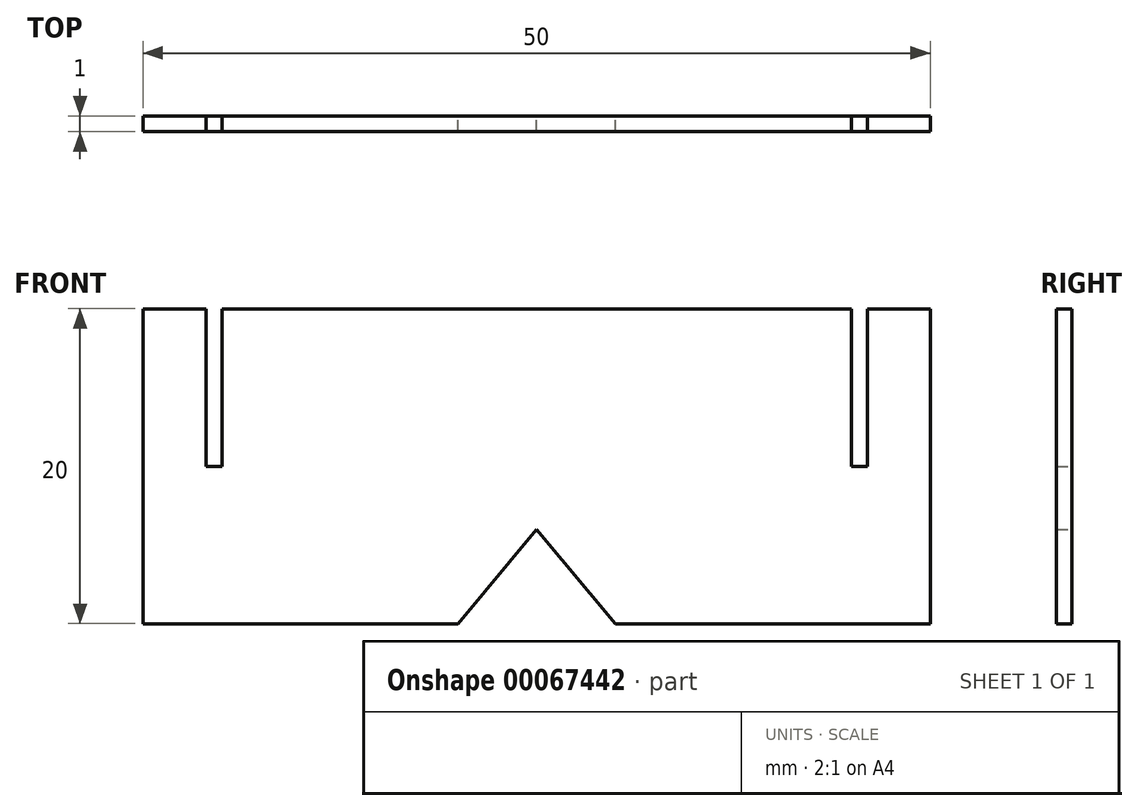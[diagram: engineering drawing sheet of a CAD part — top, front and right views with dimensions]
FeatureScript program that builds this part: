
annotation { "Feature Type Name" : "Feature", "Feature Type Description" : "" }
export const myFeature = defineFeature(function(context is Context, id is Id, definition is map)
    precondition{}
    {
        {
            var Q0;
            Q0=qCreatedBy(makeId("Front.planeOp"),FACE);
            var sketch = newSketch(context, id + "F0", { "sketchPlane" : qUnion([Q0])});
            skLineSegment(sketch, "E0.bottom", {"start": v(-29.64, 26.4) * mm, "end": v(-25.64, 26.4) * mm});
            skLineSegment(sketch, "E0.top", {"start": v(-29.64, 6.4) * mm, "end": v(-9.64, 6.4) * mm});
            skLineSegment(sketch, "E0.left", {"start": v(-29.64, 26.4) * mm, "end": v(-29.64, 6.4) * mm});
            skLineSegment(sketch, "E0.right", {"start": v(20.36, 26.4) * mm, "end": v(20.36, 6.4) * mm});
            skLineSegment(sketch, "E1.top", {"start": v(-25.64, 16.4) * mm, "end": v(-24.64, 16.4) * mm});
            skLineSegment(sketch, "E1.left", {"start": v(-25.64, 26.4) * mm, "end": v(-25.64, 16.4) * mm});
            skLineSegment(sketch, "E1.right", {"start": v(-24.64, 26.4) * mm, "end": v(-24.64, 16.4) * mm});
            skLineSegment(sketch, "E2.MirrorCS", {"start": v(15.36, 26.4) * mm, "end": v(15.36, 16.4) * mm});
            skLineSegment(sketch, "E3.MirrorCS", {"start": v(16.36, 26.4) * mm, "end": v(16.36, 16.4) * mm});
            skLineSegment(sketch, "E4.MirrorCS", {"start": v(16.36, 16.4) * mm, "end": v(15.36, 16.4) * mm});
            skPoint(sketch, "E5", {"position": v(-9.64, 6.4) * mm});
            skPoint(sketch, "E6", {"position": v(0.36, 6.4) * mm});
            skPoint(sketch, "E7", {"position": v(-4.64, 12.4) * mm});
            skLineSegment(sketch, "E8", {"start": v(-9.64, 6.4) * mm, "end": v(-4.64, 12.4) * mm});
            skLineSegment(sketch, "E9", {"start": v(-4.64, 12.4) * mm, "end": v(0.36, 6.4) * mm});
            skLineSegment(sketch, "E10.trimOffspring", {"start": v(0.36, 6.4) * mm, "end": v(20.36, 6.4) * mm});
            skLineSegment(sketch, "E11.trimOffspring", {"start": v(16.36, 26.4) * mm, "end": v(20.36, 26.4) * mm});
            skLineSegment(sketch, "E12.trimOffspring", {"start": v(-24.64, 26.4) * mm, "end": v(15.36, 26.4) * mm});
            skSolve(sketch);
        }
        {
            var Q0;
            Q0 = qSketchRegion(id + "F0", true);
            extrude(context, id + "F1", {"entities" : qUnion([Q0]), "depth" : 1 * mm});
        }
    });
